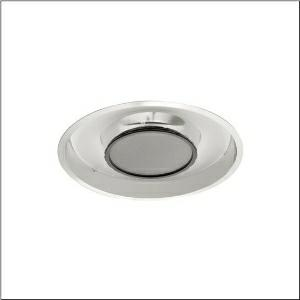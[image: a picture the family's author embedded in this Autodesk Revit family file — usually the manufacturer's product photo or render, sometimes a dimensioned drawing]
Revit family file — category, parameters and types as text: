
# Revit family: lunis_11_r_5lr610d4ob11af
name_source: partatom
category: Lighting Fixtures
units: mm (PartAtom-declared; Revit-internal decimal feet)

## family parameters
Cut with Voids When Loaded = No
Host = Face
Light Source = No
Part Type = Normal
Room Calculation Point = No
Round Connector Dimension = Use Diameter
Shared = No

## types (1)
- --- (1 x LED 4000K / CRI = 80 (unbekannt), 4860 lm, 4000K)
    Apparent Load = 37 VA
    CIE Flux Codes = 60 90 99 100 100
    Color Rendering = 80
    Color Temperature = 4000K
    Default Elevation = 1800 mm
    Description = Lunis 11 R, downlight, light control with reflector, of ultra-pure aluminium (Al 99.98%), highly specular, perforated, light emission: direct distribution, LED rated luminous flux: 4.860lm, light colour: 840, control gear: ECG Multilumen, with terminal, 3+2-pole, max. 2.5mm², mains connection: 230V, AC, 50/60Hz, diameter: 398mm, central ring, of plastic, graphite (RAL 7037), central module, blanking cover, of sheet steel, perforated, metallic grey (RAL 9006), protection rating (complete): IP20, insulation class (complete): insulation class II (safety insulation), certification: CE, ENEC, VDE, protection symbol: F, permissible ambient temperature for indoor applications: +10..+35°C, standard: EN 50419, packaging unit: 1 piece
    Height = 0 mm  [stored 0 ft]
    Lamp = 1 x LED 4000K / CRI >= 80 (unbekannt)
    Lamp Light Flux = 4860 lm
    Lamp count = 1
    Length = 398 mm
    Luminous efficacy = 131 lm/W
    Manufacturer = Siteco
    ModVariant = No
    Model = 5LR610D4OB11AF
    Mounting Place = Ceiling
    Mounting Type = Recessed
    Number of Poles = 1
    OnlyDefault = Yes
    Power Factor = 1
    Product Name = Lunis 11 R
    Product group = downlight
    ProductGroupID = 401
    Protection Class = Protection class II
    Protection Degree = IP 20
    RLX_Detail_Level = 1
    RLX_Emergency_Light_Flux = 0 lm
    RLX_Emergency_Type = 0
    RLX_Emergency_Type_DB = No
    RlxData = <blob elided: 94693 chars, md5=929c2cdf>
    Socket = socket
    Standby Power = 0 W
    System Light Flux = 4860 lm
    System Power = 37 W
    Type Comments = factory setting: High Lumen Output
    Type Image = l_1003323.jpg
    URL = http://relux.com
    VarID = @adj_196003
    Voltage = 0 V
    Weight = 0.00 kg
    Width = 0 mm  [stored 0 ft]

note: [stored X ft] marks values corroborated as IEEE doubles in the binary element streams (Revit-internal decimal feet)

## geometry (parser evidence)
native form markers: Blend x4, Sweep x13
no freeform markers — native parametric forms only
